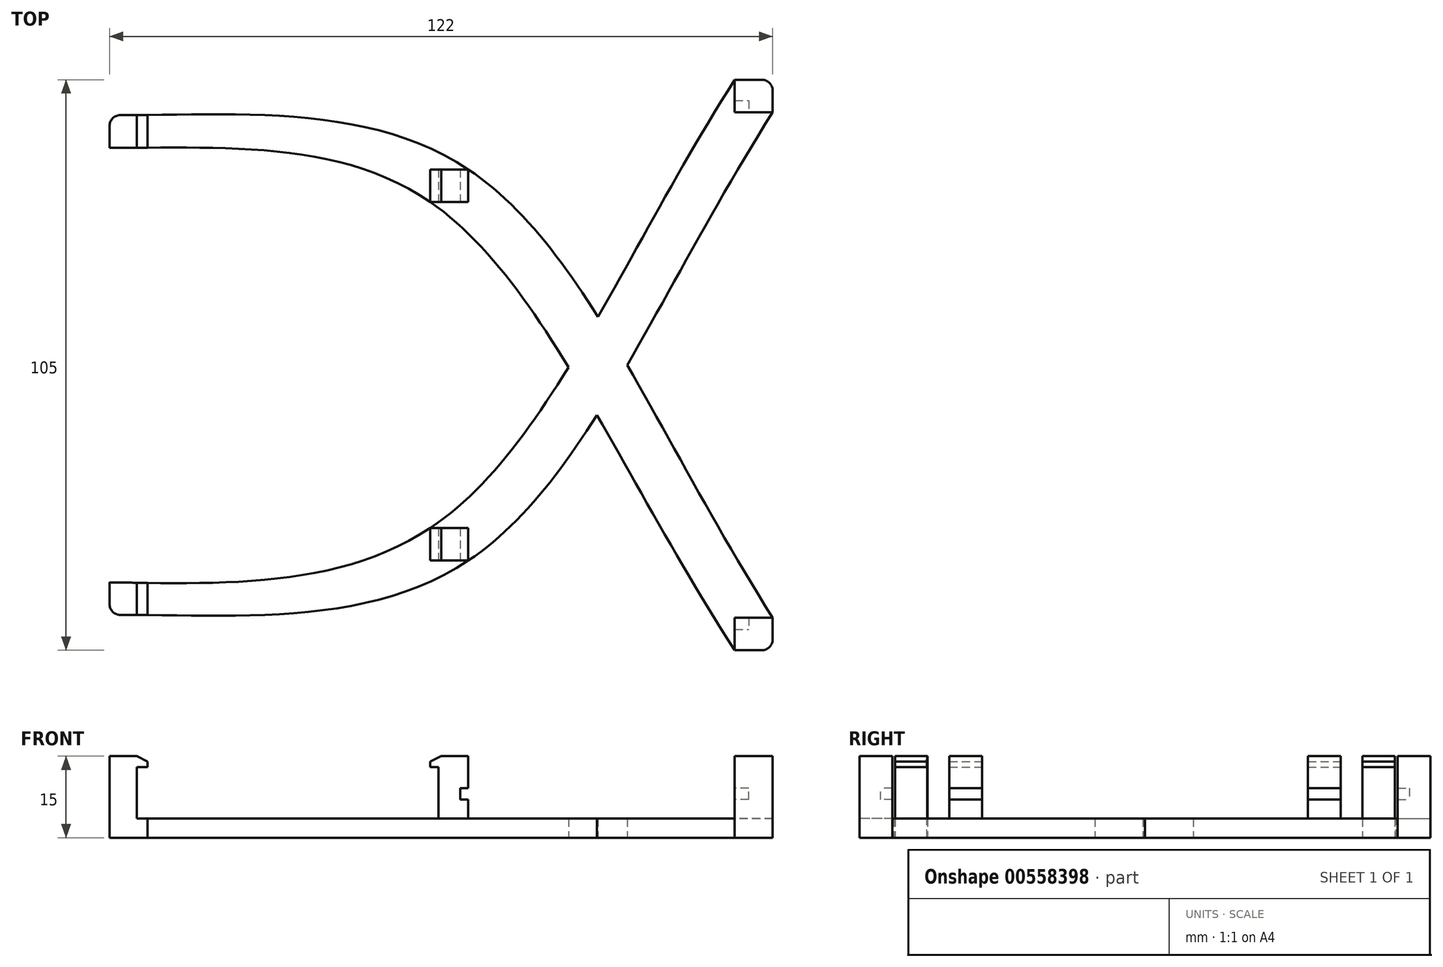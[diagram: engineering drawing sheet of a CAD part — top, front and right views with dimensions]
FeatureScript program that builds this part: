
annotation { "Feature Type Name" : "Feature", "Feature Type Description" : "" }
export const myFeature = defineFeature(function(context is Context, id is Id, definition is map)
    precondition{}
    {
        {
            var Q0;
            Q0=qCreatedBy(makeId("Top.planeOp"),FACE);
            var sketch = newSketch(context, id + "F0", { "sketchPlane" : qUnion([Q0])});
            skLineSegment(sketch, "E0.bottom", {"start": v(-62.5, 46) * mm, "end": v(-55.5, 46) * mm});
            skLineSegment(sketch, "E0.top", {"start": v(-62.5, 40) * mm, "end": v(-55.5, 40) * mm});
            skLineSegment(sketch, "E0.left", {"start": v(-62.5, 46) * mm, "end": v(-62.5, 40) * mm});
            skLineSegment(sketch, "E0.right", {"start": v(-55.5, 46) * mm, "end": v(-55.5, 40) * mm});
            skLineSegment(sketch, "E1.bottom", {"start": v(-3.5, 36) * mm, "end": v(3.5, 36) * mm});
            skLineSegment(sketch, "E1.top", {"start": v(-3.5, 30) * mm, "end": v(3.5, 30) * mm});
            skLineSegment(sketch, "E1.left", {"start": v(-3.5, 36) * mm, "end": v(-3.5, 30) * mm});
            skLineSegment(sketch, "E1.right", {"start": v(3.5, 36) * mm, "end": v(3.5, 30) * mm});
            skLineSegment(sketch, "E2.bottom", {"start": v(-3.5, -30) * mm, "end": v(3.5, -30) * mm});
            skLineSegment(sketch, "E2.top", {"start": v(-3.5, -36) * mm, "end": v(3.5, -36) * mm});
            skLineSegment(sketch, "E2.left", {"start": v(-3.5, -30) * mm, "end": v(-3.5, -36) * mm});
            skLineSegment(sketch, "E2.right", {"start": v(3.5, -30) * mm, "end": v(3.5, -36) * mm});
            skPoint(sketch, "E3", {"position": v(0, 36) * mm});
            skPoint(sketch, "E4", {"position": v(0, -30) * mm});
            skLineSegment(sketch, "E5.MirrorCS", {"start": v(-55.5, -46) * mm, "end": v(-55.5, -40) * mm});
            skLineSegment(sketch, "E6.MirrorCS", {"start": v(-62.5, -46) * mm, "end": v(-62.5, -40) * mm});
            skLineSegment(sketch, "E7.MirrorCS", {"start": v(-62.5, -46) * mm, "end": v(-55.5, -46) * mm});
            skLineSegment(sketch, "E8.MirrorCS", {"start": v(-62.5, -40) * mm, "end": v(-55.5, -40) * mm});
            skLineSegment(sketch, "E9.bottom", {"start": v(52.5, 52.5) * mm, "end": v(59.5, 52.5) * mm});
            skLineSegment(sketch, "E9.top", {"start": v(52.5, 46.5) * mm, "end": v(59.5, 46.5) * mm});
            skLineSegment(sketch, "E9.left", {"start": v(52.5, 52.5) * mm, "end": v(52.5, 46.5) * mm});
            skLineSegment(sketch, "E9.right", {"start": v(59.5, 52.5) * mm, "end": v(59.5, 46.5) * mm});
            skLineSegment(sketch, "E10.MirrorCS", {"start": v(52.5, -46.5) * mm, "end": v(59.5, -46.5) * mm});
            skLineSegment(sketch, "E11.MirrorCS", {"start": v(52.5, -52.5) * mm, "end": v(59.5, -52.5) * mm});
            skLineSegment(sketch, "E12.MirrorCS", {"start": v(52.5, -52.5) * mm, "end": v(52.5, -46.5) * mm});
            skLineSegment(sketch, "E13.MirrorCS", {"start": v(59.5, -52.5) * mm, "end": v(59.5, -46.5) * mm});
            skFitSpline(sketch, "E14", {"points": [v(-55.5, 46) * mm, v(3.5, 36) * mm, v(59.5, -46.5) * mm], "startDerivative": vector(140.44, 2.31) * mm, "endDerivative": vector(114.86, -181.01) * mm});
            skFitSpline(sketch, "E15", {"points": [v(-55.5, 40) * mm, v(-3.5, 30) * mm, v(52.5, -52.5) * mm], "startDerivative": vector(130.44, 0.39) * mm, "endDerivative": vector(114.48, -178.07) * mm});
            skFitSpline(sketch, "E16", {"points": [v(-62.5, -40) * mm, v(-3.5, -30) * mm, v(52.5, 52.5) * mm], "startDerivative": vector(140.44, -2.31) * mm, "endDerivative": vector(114.86, 181.01) * mm});
            skFitSpline(sketch, "E17", {"points": [v(-55.5, -46) * mm, v(3.5, -36) * mm, v(59.5, 46.5) * mm], "startDerivative": vector(140.44, -2.31) * mm, "endDerivative": vector(114.86, 181.01) * mm});
            skSolve(sketch);
        }
        {
            var Q0;
            Q0=makeQuery(id+"F0.imprint","IMPRINT",FACE,{"disambiguationData":[TD([[makeQuery(id+"F0.imprint","IMPRINT",EDGE,{"derivedFrom":sQuery(id+"F0.wireOp",EDGE,"E0.bottom")}),-1.0]])]});
            var Q1;
            {var subQ1=sQuery(id+"F0.wireOp",EDGE,"E0.right");Q1=makeQuery(id+"F0.imprint","IMPRINT",FACE,{"disambiguationData":[TD([[makeQuery(id+"F0.imprint","IMPRINT",EDGE,{"derivedFrom":subQ1}),1.0]])]});}
            var Q2;
            Q2=makeQuery(id+"F0.imprint","IMPRINT",FACE,{"disambiguationData":[TD([[makeQuery(id+"F0.imprint","IMPRINT",EDGE,{"derivedFrom":sQuery(id+"F0.wireOp",EDGE,"E1.bottom")}),-1.0]])]});
            var Q3;
            {var subQ5=sQuery(id+"F0.wireOp",EDGE,"E1.top");Q3=makeQuery(id+"F0.imprint","IMPRINT",FACE,{"disambiguationData":[TD([[makeQuery(id+"F0.imprint","IMPRINT",EDGE,{"derivedFrom":subQ5}),-1.0]])]});}
            var Q4;
            {var subQ0=sQuery(id+"F0.wireOp",EDGE,"E16");var subQ1=sQuery(id+"F0.wireOp",EDGE,"E14");var subQ2=makeQuery(id+"F0.imprint","INTERSECT",VERTEX,{"derivedFrom":[subQ1,subQ0]});Q4=makeQuery(id+"F0.imprint","IMPRINT",FACE,{"disambiguationData":[TD([[makeQuery(id+"F0.imprint","IMPRINT",EDGE,{"disambiguationData":[TD([[subQ2,-1.0]])],"derivedFrom":subQ1}),-1.0]])]});}
            var Q5;
            {var subQ6=sQuery(id+"F0.wireOp",EDGE,"E9.top");Q5=makeQuery(id+"F0.imprint","IMPRINT",FACE,{"disambiguationData":[TD([[makeQuery(id+"F0.imprint","IMPRINT",EDGE,{"derivedFrom":subQ6}),-1.0]])]});}
            var Q6;
            {var subQ4=sQuery(id+"F0.wireOp",EDGE,"E10.MirrorCS");Q6=makeQuery(id+"F0.imprint","IMPRINT",FACE,{"disambiguationData":[TD([[makeQuery(id+"F0.imprint","IMPRINT",EDGE,{"derivedFrom":subQ4}),1.0]])]});}
            var Q7;
            {var subQ1=sQuery(id+"F0.wireOp",EDGE,"E2.bottom");Q7=makeQuery(id+"F0.imprint","IMPRINT",FACE,{"disambiguationData":[TD([[makeQuery(id+"F0.imprint","IMPRINT",EDGE,{"derivedFrom":subQ1}),1.0]])]});}
            var Q8;
            Q8=makeQuery(id+"F0.imprint","IMPRINT",FACE,{"disambiguationData":[TD([[makeQuery(id+"F0.imprint","IMPRINT",EDGE,{"derivedFrom":sQuery(id+"F0.wireOp",EDGE,"E9.bottom")}),-1.0]])]});
            var Q9;
            Q9=makeQuery(id+"F0.imprint","IMPRINT",FACE,{"disambiguationData":[TD([[makeQuery(id+"F0.imprint","IMPRINT",EDGE,{"derivedFrom":sQuery(id+"F0.wireOp",EDGE,"E10.MirrorCS")}),-1.0]])]});
            var Q10;
            Q10=makeQuery(id+"F0.imprint","IMPRINT",FACE,{"disambiguationData":[TD([[makeQuery(id+"F0.imprint","IMPRINT",EDGE,{"derivedFrom":sQuery(id+"F0.wireOp",EDGE,"E2.bottom")}),-1.0]])]});
            var Q11;
            {var subQ6=sQuery(id+"F0.wireOp",EDGE,"E2.top");Q11=makeQuery(id+"F0.imprint","IMPRINT",FACE,{"disambiguationData":[TD([[makeQuery(id+"F0.imprint","IMPRINT",EDGE,{"derivedFrom":subQ6}),-1.0]])]});}
            var Q12;
            {var subQ4=sQuery(id+"F0.wireOp",EDGE,"E6.MirrorCS");Q12=makeQuery(id+"F0.imprint","IMPRINT",FACE,{"disambiguationData":[TD([[makeQuery(id+"F0.imprint","IMPRINT",EDGE,{"derivedFrom":subQ4}),-1.0]])]});}
            extrude(context, id + "F1", {"entities" : qUnion([Q0, Q1, Q2, Q3, Q4, Q5, Q6, Q7, Q8, Q9, Q10, Q11, Q12]), "depth" : 3.5 * mm, "offsetDistance" : 25 * mm});
        }
        {
            var Q0;
            Q0=makeQuery(id+"F0.imprint","IMPRINT",FACE,{"disambiguationData":[TD([[makeQuery(id+"F0.imprint","IMPRINT",EDGE,{"derivedFrom":sQuery(id+"F0.wireOp",EDGE,"E0.bottom")}),-1.0]])]});
            var Q1;
            Q1=makeQuery(id+"F0.imprint","IMPRINT",FACE,{"disambiguationData":[TD([[makeQuery(id+"F0.imprint","IMPRINT",EDGE,{"derivedFrom":sQuery(id+"F0.wireOp",EDGE,"E1.bottom")}),-1.0]])]});
            var Q2;
            {var subQ4=sQuery(id+"F0.wireOp",EDGE,"E6.MirrorCS");Q2=makeQuery(id+"F0.imprint","IMPRINT",FACE,{"disambiguationData":[TD([[makeQuery(id+"F0.imprint","IMPRINT",EDGE,{"derivedFrom":subQ4}),-1.0]])]});}
            var Q3;
            Q3=makeQuery(id+"F0.imprint","IMPRINT",FACE,{"disambiguationData":[TD([[makeQuery(id+"F0.imprint","IMPRINT",EDGE,{"derivedFrom":sQuery(id+"F0.wireOp",EDGE,"E2.bottom")}),-1.0]])]});
            var Q4;
            Q4=makeQuery(id+"F0.imprint","IMPRINT",FACE,{"disambiguationData":[TD([[makeQuery(id+"F0.imprint","IMPRINT",EDGE,{"derivedFrom":sQuery(id+"F0.wireOp",EDGE,"E9.bottom")}),-1.0]])]});
            var Q5;
            Q5=makeQuery(id+"F0.imprint","IMPRINT",FACE,{"disambiguationData":[TD([[makeQuery(id+"F0.imprint","IMPRINT",EDGE,{"derivedFrom":sQuery(id+"F0.wireOp",EDGE,"E10.MirrorCS")}),-1.0]])]});
            extrude(context, id + "F2", {"entities" : qUnion([Q0, Q1, Q2, Q3, Q4, Q5]), "operationType" : NewBodyOperationType.ADD, "depth" : 15 * mm, "offsetDistance" : 25 * mm});
        }
        {
            var Q0;
            Q0=qCreatedBy(makeId("Front.planeOp"),FACE);
            var sketch = newSketch(context, id + "F3", { "sketchPlane" : qUnion([Q0])});
            skLineSegment(sketch, "E18.bottom", {"start": v(-57.5, 13) * mm, "end": v(-2, 13) * mm});
            skLineSegment(sketch, "E18.top", {"start": v(-57.5, 3.5) * mm, "end": v(-2, 3.5) * mm});
            skLineSegment(sketch, "E18.left", {"start": v(-57.5, 13) * mm, "end": v(-57.5, 3.5) * mm});
            skLineSegment(sketch, "E18.right", {"start": v(-2, 13) * mm, "end": v(-2, 3.5) * mm});
            skLineSegment(sketch, "E19.bottom", {"start": v(2, 9.1) * mm, "end": v(55.1, 9.1) * mm});
            skLineSegment(sketch, "E19.top", {"start": v(2, 7) * mm, "end": v(55.1, 7) * mm});
            skLineSegment(sketch, "E19.left", {"start": v(2, 9.1) * mm, "end": v(2, 7) * mm});
            skLineSegment(sketch, "E19.right", {"start": v(55.1, 9.1) * mm, "end": v(55.1, 7) * mm});
            skSolve(sketch);
        }
        {
            var Q0;
            Q0=makeQuery(id+"F3.imprint","IMPRINT",FACE,{"disambiguationData":[TD([[makeQuery(id+"F3.imprint","IMPRINT",EDGE,{"derivedFrom":sQuery(id+"F3.wireOp",EDGE,"E18.bottom")}),-1.0]])]});
            extrude(context, id + "F4", {"entities" : qUnion([Q0]), "operationType" : NewBodyOperationType.REMOVE, "endBound" : BoundingType.SYMMETRIC, "oppositeDirection" : true, "depth" : 200 * mm, "offsetDistance" : 25 * mm});
        }
        {
            var Q0;
            Q0=makeQuery(id+"F3.imprint","IMPRINT",FACE,{"disambiguationData":[TD([[makeQuery(id+"F3.imprint","IMPRINT",EDGE,{"derivedFrom":sQuery(id+"F3.wireOp",EDGE,"E19.bottom")}),-1.0]])]});
            extrude(context, id + "F5", {"entities" : qUnion([Q0]), "operationType" : NewBodyOperationType.REMOVE, "endBound" : BoundingType.SYMMETRIC, "oppositeDirection" : true, "depth" : 97.3 * mm, "offsetDistance" : 25 * mm});
        }
        {
            var Q0;
            Q0=makeQuery(id+"F2.opExtrude","CAP_EDGE",EDGE,{"disambiguationData":[OSD([sQuery(id+"F0.wireOp",EDGE,"E1.left")])],"isStart":false});
            var Q1;
            Q1=makeQuery(id+"F2.opExtrude","CAP_EDGE",EDGE,{"disambiguationData":[OSD([sQuery(id+"F0.wireOp",EDGE,"E2.left")])],"isStart":false});
            var Q2;
            Q2=makeQuery(id+"F2.opExtrude","CAP_EDGE",EDGE,{"disambiguationData":[OSD([sQuery(id+"F0.wireOp",EDGE,"E5.MirrorCS")])],"isStart":false});
            chamfer(context, id + "F6", {"entities" : qUnion([Q0, Q1, Q2]), "chamferType" : ChamferType.TWO_OFFSETS, "width1" : 2 * mm, "oppositeDirection" : false, "width2" : 1 * mm, "tangentPropagation" : true});
        }
        {
            var Q0;
            Q0=makeQuery(id+"F2.opExtrude","CAP_EDGE",EDGE,{"disambiguationData":[OSD([sQuery(id+"F0.wireOp",EDGE,"E0.right")])],"isStart":false});
            chamfer(context, id + "F7", {"entities" : qUnion([Q0]), "chamferType" : ChamferType.TWO_OFFSETS, "width1" : 1 * mm, "oppositeDirection" : false, "width2" : 2 * mm, "tangentPropagation" : true});
        }
        {
            var Q0;
            {var subQ0=sQuery(id+"F0.wireOp",EDGE,"E9.right");var subQ1=sQuery(id+"F0.wireOp",EDGE,"E9.bottom");Q0=makeQuery(id+"F2.boolean.opBoolean","MERGE",EDGE,{"derivedFrom":[makeQuery(id+"F1.opExtrude","SWEPT_EDGE",EDGE,{"disambiguationData":[OSD([subQ1,subQ0])]}),makeQuery(id+"F2.opExtrude","SWEPT_EDGE",EDGE,{"disambiguationData":[OSD([subQ1,subQ0])]})]});}
            var Q1;
            {var subQ0=sQuery(id+"F0.wireOp",EDGE,"E13.MirrorCS");var subQ1=sQuery(id+"F0.wireOp",EDGE,"E11.MirrorCS");Q1=makeQuery(id+"F2.boolean.opBoolean","MERGE",EDGE,{"derivedFrom":[makeQuery(id+"F1.opExtrude","SWEPT_EDGE",EDGE,{"disambiguationData":[OSD([subQ1,subQ0])]}),makeQuery(id+"F2.opExtrude","SWEPT_EDGE",EDGE,{"disambiguationData":[OSD([subQ1,subQ0])]})]});}
            var Q2;
            {var subQ0=sQuery(id+"F0.wireOp",EDGE,"E7.MirrorCS");var subQ1=sQuery(id+"F0.wireOp",EDGE,"E6.MirrorCS");Q2=makeQuery(id+"F2.boolean.opBoolean","MERGE",EDGE,{"derivedFrom":[makeQuery(id+"F1.opExtrude","SWEPT_EDGE",EDGE,{"disambiguationData":[OSD([subQ1,subQ0])]}),makeQuery(id+"F2.opExtrude","SWEPT_EDGE",EDGE,{"disambiguationData":[OSD([subQ1,subQ0])]})]});}
            var Q3;
            {var subQ0=sQuery(id+"F0.wireOp",EDGE,"E0.left");var subQ1=sQuery(id+"F0.wireOp",EDGE,"E0.bottom");Q3=makeQuery(id+"F2.boolean.opBoolean","MERGE",EDGE,{"derivedFrom":[makeQuery(id+"F1.opExtrude","SWEPT_EDGE",EDGE,{"disambiguationData":[OSD([subQ1,subQ0])]}),makeQuery(id+"F2.opExtrude","SWEPT_EDGE",EDGE,{"disambiguationData":[OSD([subQ1,subQ0])]})]});}
            fillet(context, id + "F8", {"entities" : qUnion([Q0, Q1, Q2, Q3]), "radius" : 2 * mm, "tangentPropagation" : true, "allowEdgeOverflow" : false});
        }
    });
